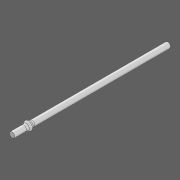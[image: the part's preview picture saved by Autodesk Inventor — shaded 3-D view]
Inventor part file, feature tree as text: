
AUTODESK INVENTOR PART (.ipt)
format: ipt  version: 2020 (Build 240168000, 168)  size: 99,328 bytes
history: native  units: in
note: dims shown in document units (in); Inventor stores cm internally (conversion verified against a paired STEP export)
features: revolve x1, fillet x1, sketch x1
ambient origin geometry x8: Origin, YZ Plane, XZ Plane, XY Plane, X Axis, Y Axis, Z Axis, Center Point
bodies: Solid1 (feature_tree)
feature tree (3):
  revolve  "Revolution1"  [1 undecoded]
  fillet  "Fillet2"  Radius=0.1969in
  sketch  "Sketch1"  dims[d0=90.0deg d5=7.0866in d8=0.1969in d12=0.2362in d14=0.5906in d15=0.2756in d17=0.1969in]
note: 1 required parameter value undecoded (feature->parameter linkage not recoverable at this tier; creation-order binding heuristic only, values carry confidence <= 0.55)
